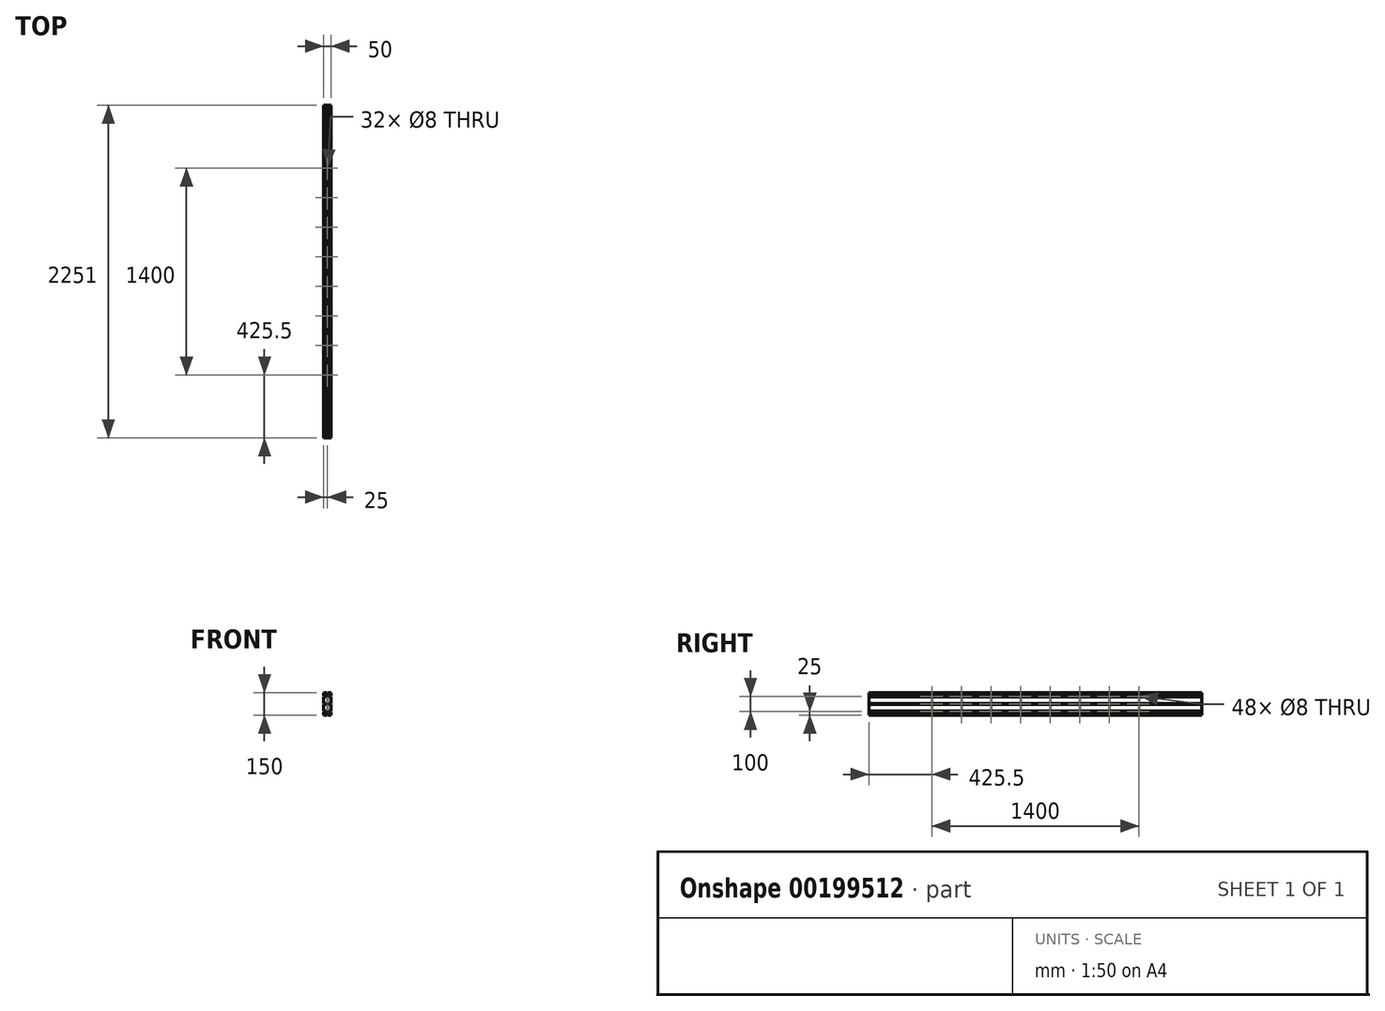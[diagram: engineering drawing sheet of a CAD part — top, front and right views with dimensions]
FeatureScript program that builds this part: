
annotation { "Feature Type Name" : "Feature", "Feature Type Description" : "" }
export const myFeature = defineFeature(function(context is Context, id is Id, definition is map)
    precondition{}
    {
        {
            var Q0;
            Q0=qCreatedBy(makeId("Front.planeOp"),FACE);
            var sketch = newSketch(context, id + "F0", { "sketchPlane" : qUnion([Q0])});
            skLineSegment(sketch, "E0.bottom", {"start": v(25, -75) * mm, "end": v(-25, -75) * mm});
            skLineSegment(sketch, "E0.top", {"start": v(25, 75) * mm, "end": v(-25, 75) * mm});
            skLineSegment(sketch, "E0.left", {"start": v(25, -75) * mm, "end": v(25, 75) * mm});
            skLineSegment(sketch, "E0.right", {"start": v(-25, -75) * mm, "end": v(-25, 75) * mm});
            skPoint(sketch, "E0.middle", {"position": v(0, 0) * mm});
            skSolve(sketch);
        }
        {
            var Q0;
            Q0=qSketchRegion(id+"F0",true);
            extrude(context, id + "F1", {"entities" : qUnion([Q0]), "depth" : 2251 * mm});
        }
        {
            var Q0;
            Q0=makeQuery(id+"F1.opExtrude","SWEPT_FACE",FACE,{"disambiguationData":[OSD([sQuery(id+"F0.wireOp",EDGE,"E0.left")])]});
            var sketch = newSketch(context, id + "F2", { "sketchPlane" : qUnion([Q0])});
            skLineSegment(sketch, "E1", {"start": v(-2251, 0) * mm, "end": v(-640.44, 0) * mm, "construction": true});
            skCircle(sketch, "E2", {"center": v(-1825.5, 50) * mm, "radius": 4 * mm});
            skCircle(sketch, "E3.1.0.0", {"center": v(-1625.5, 50) * mm, "radius": 4 * mm});
            skCircle(sketch, "E3.2.0.0", {"center": v(-1425.5, 50) * mm, "radius": 4 * mm});
            skCircle(sketch, "E3.3.0.0", {"center": v(-1225.5, 50) * mm, "radius": 4 * mm});
            skCircle(sketch, "E3.4.0.0", {"center": v(-1025.5, 50) * mm, "radius": 4 * mm});
            skLineSegment(sketch, "E3.direction1", {"start": v(-1825.5, 50) * mm, "end": v(-1625.5, 50) * mm, "construction": true});
            skCircle(sketch, "E4.0.5.0", {"center": v(-825.5, 50) * mm, "radius": 4 * mm});
            skCircle(sketch, "E4.0.6.0", {"center": v(-625.5, 50) * mm, "radius": 4 * mm});
            skCircle(sketch, "E4.0.7.0", {"center": v(-425.5, 50) * mm, "radius": 4 * mm});
            skCircle(sketch, "E5.MirrorC", {"center": v(-1625.5, -50) * mm, "radius": 4 * mm});
            skCircle(sketch, "E6.MirrorC", {"center": v(-1425.5, -50) * mm, "radius": 4 * mm});
            skCircle(sketch, "E7.MirrorC", {"center": v(-1225.5, -50) * mm, "radius": 4 * mm});
            skCircle(sketch, "E8.MirrorC", {"center": v(-425.5, -50) * mm, "radius": 4 * mm});
            skCircle(sketch, "E9.MirrorC", {"center": v(-625.5, -50) * mm, "radius": 4 * mm});
            skCircle(sketch, "E10.MirrorC", {"center": v(-1025.5, -50) * mm, "radius": 4 * mm});
            skCircle(sketch, "E11.MirrorC", {"center": v(-825.5, -50) * mm, "radius": 4 * mm});
            skCircle(sketch, "E12.MirrorC", {"center": v(-1825.5, -50) * mm, "radius": 4 * mm});
            skCircle(sketch, "E13", {"center": v(-1825.5, 0) * mm, "radius": 4 * mm});
            skCircle(sketch, "E14.1.0.0", {"center": v(-1625.5, 0) * mm, "radius": 4 * mm});
            skCircle(sketch, "E14.2.0.0", {"center": v(-1425.5, 0) * mm, "radius": 4 * mm});
            skLineSegment(sketch, "E14.direction1", {"start": v(-1825.5, 0) * mm, "end": v(-1625.5, 0) * mm, "construction": true});
            skCircle(sketch, "E15.0.3.0", {"center": v(-1225.5, 0) * mm, "radius": 4 * mm});
            skCircle(sketch, "E15.0.4.0", {"center": v(-1025.5, 0) * mm, "radius": 4 * mm});
            skCircle(sketch, "E15.0.5.0", {"center": v(-825.5, 0) * mm, "radius": 4 * mm});
            skCircle(sketch, "E15.0.6.0", {"center": v(-625.5, 0) * mm, "radius": 4 * mm});
            skCircle(sketch, "E15.0.7.0", {"center": v(-425.5, 0) * mm, "radius": 4 * mm});
            skLineSegment(sketch, "E16", {"start": v(-1225.5, 50) * mm, "end": v(-1025.5, 50) * mm, "construction": true});
            skLineSegment(sketch, "E17", {"start": v(-1125.5, 50) * mm, "end": v(-1125.5, -75) * mm, "construction": true});
            skLineSegment(sketch, "E18", {"start": v(-1825.5, 50) * mm, "end": v(-1825.5, 0) * mm, "construction": true});
            skSolve(sketch);
        }
        {
            var Q0;
            Q0=qSketchRegion(id+"F2",true);
            extrude(context, id + "F3", {"entities" : qUnion([Q0]), "operationType" : NewBodyOperationType.REMOVE, "endBound" : BoundingType.THROUGH_ALL, "oppositeDirection" : true, "depth" : 25 * mm});
        }
        {
            var Q0;
            Q0=makeQuery(id+"F1.opExtrude","SWEPT_FACE",FACE,{"disambiguationData":[OSD([sQuery(id+"F0.wireOp",EDGE,"E0.bottom")])]});
            var sketch = newSketch(context, id + "F4", { "sketchPlane" : qUnion([Q0])});
            skLineSegment(sketch, "E19", {"start": v(0, 2251) * mm, "end": v(0, 1392.8) * mm, "construction": true});
            skCircle(sketch, "E20", {"center": v(0, 1825.5) * mm, "radius": 4 * mm});
            skCircle(sketch, "E21.0.1.0", {"center": v(0, 1625.5) * mm, "radius": 4 * mm});
            skCircle(sketch, "E21.0.2.0", {"center": v(0, 1425.5) * mm, "radius": 4 * mm});
            skCircle(sketch, "E21.0.3.0", {"center": v(0, 1225.5) * mm, "radius": 4 * mm});
            skCircle(sketch, "E21.0.4.0", {"center": v(0, 1025.5) * mm, "radius": 4 * mm});
            skCircle(sketch, "E21.0.5.0", {"center": v(0, 825.5) * mm, "radius": 4 * mm});
            skCircle(sketch, "E21.0.6.0", {"center": v(0, 625.5) * mm, "radius": 4 * mm});
            skCircle(sketch, "E21.0.7.0", {"center": v(0, 425.5) * mm, "radius": 4 * mm});
            skLineSegment(sketch, "E21.direction1", {"start": v(0, 1825.5) * mm, "end": v(25, 1825.5) * mm, "construction": true});
            skLineSegment(sketch, "E21.direction2", {"start": v(0, 1825.5) * mm, "end": v(0, 1625.5) * mm, "construction": true});
            skLineSegment(sketch, "E22", {"start": v(0, 1225.5) * mm, "end": v(0, 1025.5) * mm, "construction": true});
            skLineSegment(sketch, "E23", {"start": v(0, 1125.5) * mm, "end": v(25, 1125.5) * mm, "construction": true});
            skPoint(sketch, "E23.endSnap0", {"position": v(0, 1125.5) * mm});
            skSolve(sketch);
        }
        {
            var Q0;
            Q0=qSketchRegion(id+"F4",true);
            extrude(context, id + "F5", {"entities" : qUnion([Q0]), "operationType" : NewBodyOperationType.REMOVE, "endBound" : BoundingType.THROUGH_ALL, "oppositeDirection" : true, "depth" : 25 * mm});
        }
        {
            var Q0;
            Q0=makeQuery(id+"F1.opExtrude","CAP_FACE",FACE,{"disambiguationData":[OSD([sQuery(id+"F0.wireOp",EDGE,"E0.bottom"),sQuery(id+"F0.wireOp",EDGE,"E0.top"),sQuery(id+"F0.wireOp",EDGE,"E0.left"),sQuery(id+"F0.wireOp",EDGE,"E0.right")])],"isStart":false});
            var sketch = newSketch(context, id + "F6", { "sketchPlane" : qUnion([Q0])});
            skLineSegment(sketch, "E24", {"start": v(0, 75) * mm, "end": v(0, -75) * mm, "construction": true});
            skLineSegment(sketch, "E25", {"start": v(-25, 50) * mm, "end": v(25, 50) * mm, "construction": true});
            skLineSegment(sketch, "E26.bottom", {"start": v(3, 61) * mm, "end": v(-3, 61) * mm});
            skLineSegment(sketch, "E26.top", {"start": v(3, 75) * mm, "end": v(-3, 75) * mm});
            skLineSegment(sketch, "E26.left", {"start": v(3, 61) * mm, "end": v(3, 75) * mm});
            skLineSegment(sketch, "E26.right", {"start": v(-3, 61) * mm, "end": v(-3, 75) * mm});
            skPoint(sketch, "E26.middle", {"position": v(0, 68) * mm});
            skLineSegment(sketch, "E27", {"start": v(-25, 0) * mm, "end": v(25, 0) * mm, "construction": true});
            skLineSegment(sketch, "E28.MirrorCS", {"start": v(-3, -61) * mm, "end": v(-3, -75) * mm});
            skLineSegment(sketch, "E29.MirrorCS", {"start": v(3, -75) * mm, "end": v(-3, -75) * mm});
            skLineSegment(sketch, "E30.MirrorCS", {"start": v(3, -61) * mm, "end": v(3, -75) * mm});
            skLineSegment(sketch, "E31.MirrorCS", {"start": v(3, -61) * mm, "end": v(-3, -61) * mm});
            skLineSegment(sketch, "E32.bottom", {"start": v(-25, 47) * mm, "end": v(-11, 47) * mm});
            skLineSegment(sketch, "E32.top", {"start": v(-25, 53) * mm, "end": v(-11, 53) * mm});
            skLineSegment(sketch, "E32.left", {"start": v(-25, 47) * mm, "end": v(-25, 53) * mm});
            skLineSegment(sketch, "E32.right", {"start": v(-11, 47) * mm, "end": v(-11, 53) * mm});
            skPoint(sketch, "E32.middle", {"position": v(-18, 50) * mm});
            skLineSegment(sketch, "E33.bottom", {"start": v(-25, -3) * mm, "end": v(-11, -3) * mm});
            skLineSegment(sketch, "E33.top", {"start": v(-25, 3) * mm, "end": v(-11, 3) * mm});
            skLineSegment(sketch, "E33.left", {"start": v(-25, -3) * mm, "end": v(-25, 3) * mm});
            skLineSegment(sketch, "E33.right", {"start": v(-11, -3) * mm, "end": v(-11, 3) * mm});
            skPoint(sketch, "E33.middle", {"position": v(-18, 0) * mm});
            skLineSegment(sketch, "E34.MirrorCS", {"start": v(-25, -47) * mm, "end": v(-11, -47) * mm});
            skLineSegment(sketch, "E35.MirrorCS", {"start": v(-25, -53) * mm, "end": v(-11, -53) * mm});
            skLineSegment(sketch, "E36.MirrorCS", {"start": v(-11, -47) * mm, "end": v(-11, -53) * mm});
            skLineSegment(sketch, "E37.MirrorCS", {"start": v(-25, -47) * mm, "end": v(-25, -53) * mm});
            skLineSegment(sketch, "E38.MirrorCS", {"start": v(25, 47) * mm, "end": v(11, 47) * mm});
            skLineSegment(sketch, "E39.MirrorCS", {"start": v(25, 53) * mm, "end": v(11, 53) * mm});
            skLineSegment(sketch, "E40.MirrorCS", {"start": v(11, 47) * mm, "end": v(11, 53) * mm});
            skLineSegment(sketch, "E41.MirrorCS", {"start": v(25, 47) * mm, "end": v(25, 53) * mm});
            skLineSegment(sketch, "E42.MirrorCS", {"start": v(25, -3) * mm, "end": v(11, -3) * mm});
            skLineSegment(sketch, "E43.MirrorCS", {"start": v(25, 3) * mm, "end": v(11, 3) * mm});
            skLineSegment(sketch, "E44.MirrorCS", {"start": v(11, -3) * mm, "end": v(11, 3) * mm});
            skLineSegment(sketch, "E45.MirrorCS", {"start": v(25, -3) * mm, "end": v(25, 3) * mm});
            skLineSegment(sketch, "E46.MirrorCS", {"start": v(25, -47) * mm, "end": v(11, -47) * mm});
            skLineSegment(sketch, "E47.MirrorCS", {"start": v(25, -53) * mm, "end": v(11, -53) * mm});
            skLineSegment(sketch, "E48.MirrorCS", {"start": v(11, -47) * mm, "end": v(11, -53) * mm});
            skLineSegment(sketch, "E49.MirrorCS", {"start": v(25, -47) * mm, "end": v(25, -53) * mm});
            skSolve(sketch);
        }
        {
            var Q0;
            Q0 = qSketchRegion(id + "F6", true);
            extrude(context, id + "F7", {"entities" : qUnion([Q0]), "operationType" : NewBodyOperationType.REMOVE, "endBound" : BoundingType.THROUGH_ALL, "oppositeDirection" : true, "depth" : 25 * mm});
        }
    });
